# Revit family: Accessory-Bath_Base-KOHLER-Artifacts-K-20027
name_source: partatom
category: Specialty Equipment
revit_build: Autodesk Revit 2017 (Build: 20160225_1515(x64)
units: mm (PartAtom-declared; Revit-internal decimal feet)

## family parameters
Cut with Voids When Loaded = No
Host = Face
OmniClass Number = 23.31.25.00
OmniClass Title = Toilet and Bath Specialties
Part Type = Normal
Room Calculation Point = No
Round Connector Dimension = Use Diameter
Shared = No

## types (6) — shared parameters
ADA Compliant = No
Assembly Code = C1030200
Date Modified = 02/03/2021
Default Elevation = 0"
Description = Bath base for freestanding bath
Height = 5"
Length = 51 1/4"
Manufacturer = KOHLER Co.
Master Format 2014 = 10 28 00
Master Format 2014 Name = Toilet, Bath, and Laundry Accessories
Material = Durable Hardwood Construction
Product Documentation Link = https://www.us.kohler.com
Product Name = Artifacts
Product Page URL = http://www.us.kohler.com
URL = https://www.us.kohler.com
WaterSense Certified = No
Width = 29 7/16"

## per-type parameters (varying)
| type | Finish | Model | Type |
| 0-White | Kohler-Wood-Molded-0-White | K-20027-0 | 1 |
| 96-Biscuit | Kohler-Wood-Molded-96-Biscuit | K-20027-96 | 2 |
| 7-Black Black | Kohler-Wood-Molded-7-Black_Black | K-20027-7 | 3 |
| GRL-Grey Lavender | KOHLER-Wood-GRL-Lavender_Grey | K-20027-GRL | 4 |
| DGB-Indigo Blue | KOHLER-Wood-DGB-Indigo_Blue | K-20027-DGB | 5 |
| PLM-Black Plum | KOHLER-Wood-PLM-Black_Plum | K-20027-PLM | 6 |

## geometry (parser evidence)
native form markers: Sweep x6
no freeform markers — native parametric forms only
